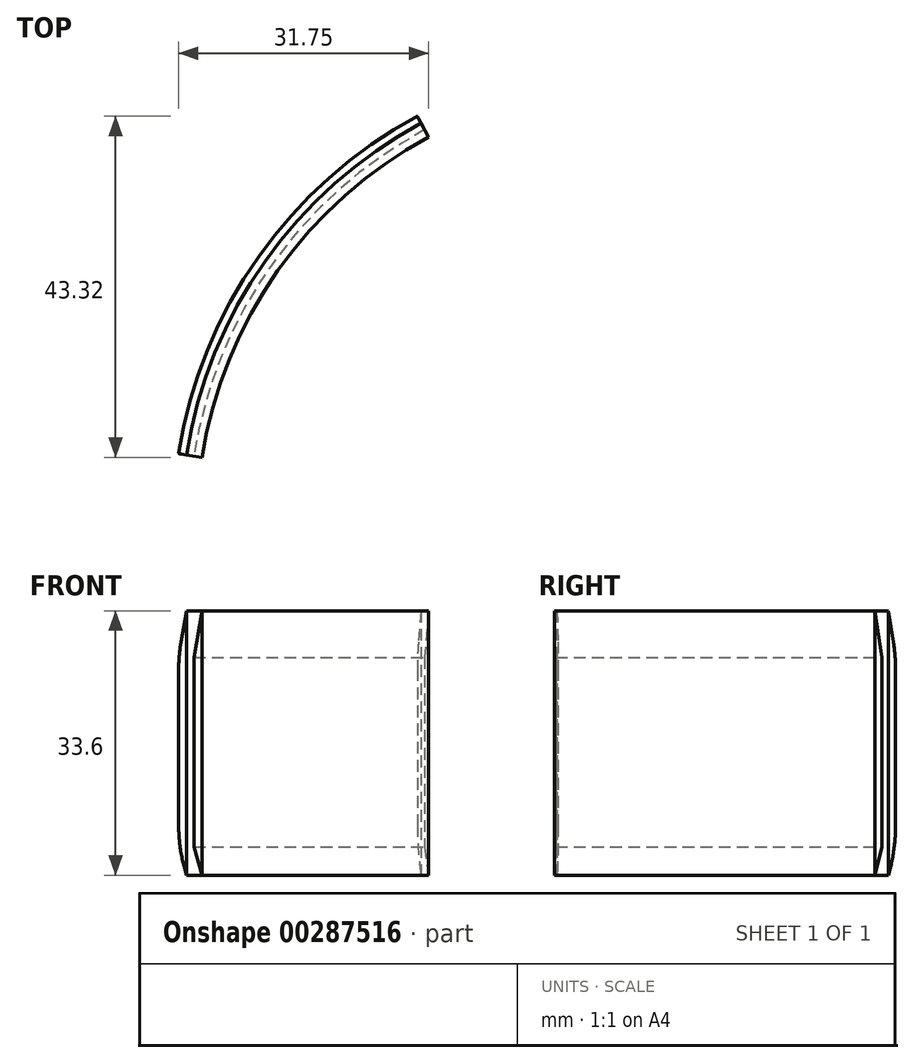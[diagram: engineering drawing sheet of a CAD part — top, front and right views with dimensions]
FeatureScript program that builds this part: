
annotation { "Feature Type Name" : "Feature", "Feature Type Description" : "" }
export const myFeature = defineFeature(function(context is Context, id is Id, definition is map)
    precondition{}
    {
        {
            var Q0;
            Q0=qCreatedBy(makeId("Top.planeOp"),FACE);
            var sketch = newSketch(context, id + "F0", { "sketchPlane" : qUnion([Q0])});
            skLineSegment(sketch, "E0", {"start": v(0, 0) * mm, "end": v(-29.8, -42.12) * mm, "construction": true});
            skSolve(sketch);
        }
        {
            var Q0;
            Q0=qCreatedBy(makeId("Top.planeOp"),FACE);
            var sketch = newSketch(context, id + "F1", { "sketchPlane" : qUnion([Q0])});
            skArc(sketch, "E1", {"start": v(0, 0) * mm, "mid": v(-19.84, -17.57) * mm, "end": v(-29.8, -42.12) * mm});
            skArc(sketch, "E2.0", {"start": v(0.95, -1.76) * mm, "mid": v(-18.2, -18.72) * mm, "end": v(-27.82, -42.43) * mm});
            skLineSegment(sketch, "E3", {"start": v(0, 0) * mm, "end": v(0.95, -1.76) * mm});
            skLineSegment(sketch, "E4", {"start": v(-29.8, -42.12) * mm, "end": v(-27.82, -42.43) * mm});
            skSolve(sketch);
        }
        {
            var Q0;
            Q0 = qSketchRegion(id + "F1", true);
            extrude(context, id + "F2", {"entities" : qUnion([Q0]), "depth" : 33.6 * mm});
        }
        {
            var Q0;
            Q0=makeQuery(id+"F2.opExtrude","SWEPT_FACE",FACE,{"disambiguationData":[OSD([sQuery(id+"F1.wireOp",EDGE,"E4")])]});
            var sketch = newSketch(context, id + "F3", { "sketchPlane" : qUnion([Q0])});
            skLineSegment(sketch, "E5", {"start": v(-22.95, 33.6) * mm, "end": v(-23.96, 27.92) * mm});
            skLineSegment(sketch, "E6", {"start": v(-23.96, 27.92) * mm, "end": v(-23.96, 3.59) * mm});
            skLineSegment(sketch, "E7", {"start": v(-23.96, 3.59) * mm, "end": v(-22.95, 0) * mm});
            skLineSegment(sketch, "E8", {"start": v(-20.95, 33.6) * mm, "end": v(-22, 27.68) * mm});
            skLineSegment(sketch, "E9", {"start": v(-22, 27.68) * mm, "end": v(-22, 3.59) * mm});
            skLineSegment(sketch, "E10", {"start": v(-22, 3.59) * mm, "end": v(-20.95, 0) * mm});
            skLineSegment(sketch, "E11", {"start": v(-20.95, 0) * mm, "end": v(-22.95, 0) * mm});
            skLineSegment(sketch, "E12", {"start": v(-20.95, 33.6) * mm, "end": v(-22.95, 33.6) * mm});
            skSolve(sketch);
        }
        {
            var Q0;
            Q0=makeQuery(id+"F3.imprint","IMPRINT",FACE,{"disambiguationData":[TD([[makeQuery(id+"F3.imprint","IMPRINT",EDGE,{"derivedFrom":sQuery(id+"F3.wireOp",EDGE,"E8")}),-1.0]])]});
            var Q1;
            Q1=makeQuery(id+"F3.imprint","IMPRINT",FACE,{"disambiguationData":[TD([[makeQuery(id+"F3.imprint","IMPRINT",EDGE,{"derivedFrom":sQuery(id+"F3.wireOp",EDGE,"E5")}),1.0]])]});
            var Q2;
            Q2=makeQuery(id+"F2.opExtrude","CAP_EDGE",EDGE,{"disambiguationData":[OSD([sQuery(id+"F1.wireOp",EDGE,"E1")])],"isStart":false});
            sweep(context, id + "F4", {"profiles" : qUnion([Q0, Q1]), "path" : qUnion([Q2])});
        }
        {
            var Q0;
            Q0=makeQuery(id+"F4.opSweep","SWEPT_EDGE",EDGE,{"disambiguationData":[OSD([sQuery(id+"F1.wireOp",EDGE,"E1"),sQuery(id+"F3.wireOp",EDGE,"E5"),sQuery(id+"F3.wireOp",EDGE,"E6")])]});
            var Q1;
            Q1=makeQuery(id+"F4.opSweep","SWEPT_EDGE",EDGE,{"disambiguationData":[OSD([sQuery(id+"F1.wireOp",EDGE,"E1"),sQuery(id+"F3.wireOp",EDGE,"E6"),sQuery(id+"F3.wireOp",EDGE,"E7")])]});
            fillet(context, id + "F5", {"entities" : qUnion([Q0, Q1]), "radius" : 20 * mm, "tangentPropagation" : true, "allowEdgeOverflow" : false});
        }
        {
            var Q0;
            Q0=makeQuery(id+"F4.opSweep","CAP_EDGE",EDGE,{"disambiguationData":[OSD([sQuery(id+"F1.wireOp",EDGE,"E1"),sQuery(id+"F1.wireOp",EDGE,"E3"),sQuery(id+"F3.wireOp",EDGE,"E9")])],"isStart":false});
            cPlane(context, id + "F6", {"entities" : qUnion([Q0]), "cplaneType" : CPlaneType.LINE_ANGLE, "offset" : 25 * mm, "angle" : 45 * degree, "width" : 150 * mm, "height" : 150 * mm});
        }
    });
